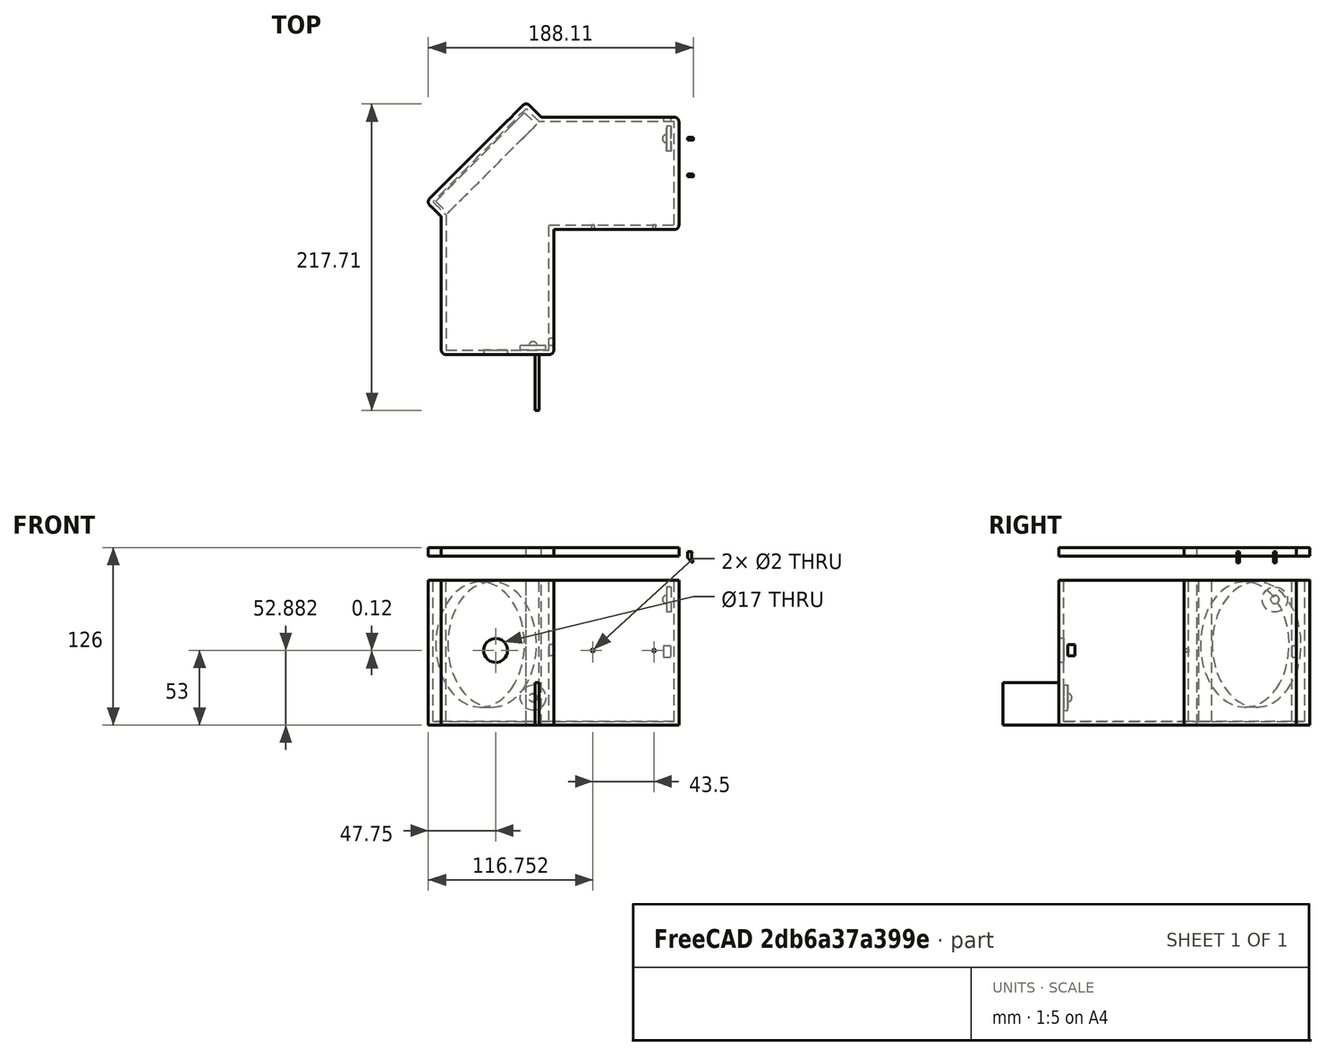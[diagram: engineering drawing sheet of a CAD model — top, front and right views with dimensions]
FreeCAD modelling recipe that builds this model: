
FCSTD DOCUMENT  (FreeCAD 0.16R)
Label: camhalter
License: All rights reserved
LicenseURL: http://en.wikipedia.org/wiki/All_rights_reserved
objects: Part::Extrusion×6, Part::Cut×6, Part::Cylinder×5, Part::Feature×5, Part::Box×3, Part::MultiFuse×2, Part::Fuse×1, Part::Sphere×1
note: 29 computed .brp shape members not serialized (recipe doc carries the construction recipe); baked Part::Feature solids carry a one-line shape summary decoded from their .brp

FEATURE [Part::Cylinder] Cylinder
  Angle = 360
  Height = 10
  Placement = pos=(49,-222,53) rot=(1,0,0;1.5708rad)
  Radius = 8.5
FEATURE [Part::Cylinder] Cylinder001  label="PetriDish"
  Angle = 360
  Height = 12
  Placement = pos=(38.0193,-87.9139,57.268) rot=(0.707107,0.707107,0;1.5708rad)
  Radius = 44.5
FEATURE [Part::Cylinder] Cylinder002  label="Cylinder001"
  Angle = 360
  Height = 10
  Radius = 1
FEATURE [Part::Cylinder] Cylinder003  label="Cylinder002"
  Angle = 360
  Height = 10
  Placement = pos=(43.5,0,0) rot=(0,0,1;0rad)
  Radius = 1
FEATURE [Part::Fuse] Fusion  label="GreenFlashMountHoles"
  Base = -> Cylinder002
  Placement = pos=(118,-135,53) rot=(0.999998,0.001797,-0.000952;1.57041rad)
  Tool = -> Cylinder003
FEATURE [Part::Cylinder] Cylinder004  label="Cylinder003"
  Angle = 360
  Height = 3
  Radius = 9
FEATURE [Part::Sphere] Sphere
  Angle1 = -90
  Angle2 = 90
  Angle3 = 360
  Placement = pos=(0,0,3) rot=(0,0,1;0rad)
  Radius = 2.9
FEATURE [Part::MultiFuse] Fusion001  label="LED"
  Placement = pos=(75.6253,-225,19.4179) rot=(-1,0,0;1.5708rad)
  Shapes = -> [Sphere,Cylinder004]
FEATURE [Part::MultiFuse] Fusion002  label="LED001"
  Placement = pos=(173.394,-74.9659,89.1908) rot=(0,-1,0;1.5708rad)
  Shapes = -> [Sphere,Cylinder004]
FEATURE [Part::Box] Box  label="Cube"
  Height = 10
  Length = 8
  Placement = pos=(94.1903,-221.986,49.0629) rot=(-0.002,-0.999998,0;1.5708rad)
  Width = 5
FEATURE [Part::Box] Box001  label="Cube001"
  Height = 10
  Length = 8
  Placement = pos=(173.226,-55.7828,48.0337) rot=(0.580134,-0.575953,0.575953;2.0944rad)
  Width = 5
FEATURE [Part::Feature] rect3373002
  shape: bbox 191.9 x 191.6 x 2e-07 mm, 0 faces, 0 solids (baked)
FEATURE [Part::Feature] rect3373003
  shape: bbox 183.3 x 183.5 x 2e-07 mm, 0 faces, 0 solids (baked)
FEATURE [Part::Feature] path3652
  shape: bbox 4.105 x 7.663 x 2e-07 mm, 0 faces, 0 solids (baked)
FEATURE [Part::Extrusion] Extrude004
  Base = -> path3652
  Dir = (0,0,2)
  Placement = pos=(260.5,-74,-38) rot=(0,0.707107,-0.707107;3.14159rad)
  Solid = true
FEATURE [Part::Extrusion] Extrude005
  Base = -> path3652
  Dir = (0,0,2)
  Placement = pos=(260.5,-100,-38) rot=(0,0.707107,-0.707107;3.14159rad)
  Solid = true
FEATURE [Part::Box] Box002  label="Cube002"
  Height = 30
  Length = 3
  Placement = pos=(77,-268,0) rot=(0,0,1;0rad)
  Width = 40
FEATURE [Part::Feature] path3148001
  shape: bbox 178.1 x 178.1 x 2e-07 mm, 0 faces, 0 solids (baked)
FEATURE [Part::Extrusion] Extrude
  Base = -> path3148001
  Dir = (0,0,103)
  Solid = true
FEATURE [Part::Extrusion] Extrude002
  Base = -> path3148001
  Dir = (0,0,6)
  Solid = true
FEATURE [Part::Feature] rect3373004
  shape: bbox 171.2 x 171.4 x 2e-07 mm, 0 faces, 0 solids (baked)
FEATURE [Part::Extrusion] Extrude001
  Base = -> rect3373004
  Dir = (0,0,103)
  Placement = pos=(0,0,2.5) rot=(0,0,1;0rad)
  Solid = true
FEATURE [Part::Cut] Cut
  Base = -> Extrude
  Tool = -> Extrude001
FEATURE [Part::Cut] Cut001
  Base = -> Cut
  Tool = -> Cylinder
FEATURE [Part::Cut] Cut002
  Base = -> Cut001
  Tool = -> Fusion
FEATURE [Part::Cut] Cut003
  Base = -> Cut002
  Tool = -> Box
FEATURE [Part::Cut] Cut004
  Base = -> Cut003
  Tool = -> Box001
FEATURE [Part::Extrusion] Extrude003
  Base = -> rect3373004
  Dir = (0,0,6)
  Placement = pos=(0,0,-2.5) rot=(0,0,1;0rad)
  Solid = true
FEATURE [Part::Cut] Cut005
  Base = -> Extrude002
  Placement = pos=(0,0,120) rot=(0,0,1;0rad)
  Tool = -> Extrude003
